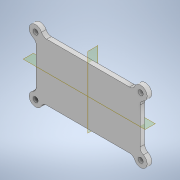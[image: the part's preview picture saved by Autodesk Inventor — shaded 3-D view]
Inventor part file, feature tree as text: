
AUTODESK INVENTOR PART (.ipt)
format: ipt  version: 2020 (Build 240168000, 168)  size: 170,496 bytes
history: native  units: in
note: dims shown in document units (in); Inventor stores cm internally (conversion verified against a paired STEP export)
features: extrude x3, sketch x3, fillet x2, plane x2, mirror x2, projected_geometry x2
ambient origin geometry x8: Origin, YZ Plane, XZ Plane, XY Plane, X Axis, Y Axis, Z Axis, Center Point
bodies: Solid1 (feature_tree)
feature tree (14):
  extrude  "Extrusion1"  Depth=1.04in
  extrude  "Extrusion2"  Depth=0.1in
  fillet  "Fillet1"  Radius=0.1in
  extrude  "Extrusion3"  Depth=0.125in
  plane  "Work Plane1"
  plane  "Work Plane2"
  mirror  "Mirror1"
  mirror  "Mirror2"
  fillet  "Fillet2"  Radius=0.14in
  sketch  "Sketch1"  dims[d0=2.05in d1=1.04in]
  sketch  "Sketch2"  dims[d2=0.1in d3=0.0in d4=0.1in d5=0.1in d6=0.0in]
  projected_geometry  "Projected Loop1"
  sketch  "Sketch4"  dims[d11=0.125in d12=0.1094in d13=0.14in d14=0.1in d15=0.0in d16=0.125in]
  projected_geometry  "Projected Loop4"
